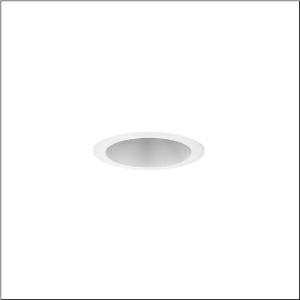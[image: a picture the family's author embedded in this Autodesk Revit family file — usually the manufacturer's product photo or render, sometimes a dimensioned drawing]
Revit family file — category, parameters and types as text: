
# Revit family: lunis_31_mini_51dn15de41
name_source: partatom
category: Lighting Fixtures
units: mm (PartAtom-declared; Revit-internal decimal feet)

## family parameters
Cut with Voids When Loaded = No
Host = Face
Light Source = No
Part Type = Normal
Room Calculation Point = No
Round Connector Dimension = Use Diameter
Shared = No

## types (1)
- Lunis 31 mini (1 x LED, 1040 lm, 8.3 W, 4000K)
    Apparent Load = 8 VA
    CIE Flux Codes = 93 98 100 100 100
    Color Rendering = 80
    Color Temperature = 4000K
    Default Elevation = 1800 mm
    Description = Lunis 31,  mini, downlight, light control with lens, light emission: direct distribution, LED rated luminous flux: 1.040lm, light colour: 840, mains connection: 220..240V, AC, 50/60Hz, housing, white, protection rating (complete): IP20, protection rating (on room side): IP54, insulation class (complete): insulation class II (safety insulation), certification: CE, packaging unit: 1 piece
    Height = 0 mm  [stored 0 ft]
    Lamp = 1 x LED
    Lamp Light Flux = 1040 lm
    Lamp Power = 8.3 W
    Lamp count = 1
    Length = 188 mm  [stored 0.616798 ft]
    Luminous efficacy = 125 lm/W
    Manufacturer = Siteco
    ModVariant = No
    Model = 51DN15DE41
    Mounting Place = Ceiling
    Mounting Type = Recessed
    Number of Poles = 1
    OnlyDefault = Yes
    Power Factor = 1
    Product Name = Lunis 31 mini
    Product group = downlight
    ProductGroupID = 400
    Protection Class = Protection class II
    Protection Degree = IP 20
    RLX_Detail_Level = 1
    RLX_Emergency_Light_Flux = 0 lm
    RLX_Emergency_Type = 0
    RLX_Emergency_Type_DB = No
    RlxData = <blob elided: 21765 chars, md5=ab6ad6cd>
    Socket = socket
    Standby Power = 0 W
    System Light Flux = 1040 lm
    System Power = 8 W
    Type Comments = Product without accessories
    Type Image = l_1005624.jpg
    URL = http://relux.com
    VarID = ---
    Voltage = 0 V
    Weight = 0.00 kg
    Width = 0 mm  [stored 0 ft]

note: [stored X ft] marks values corroborated as IEEE doubles in the binary element streams (Revit-internal decimal feet)

## geometry (parser evidence)
native form markers: Blend x4, Sweep x11
no freeform markers — native parametric forms only
